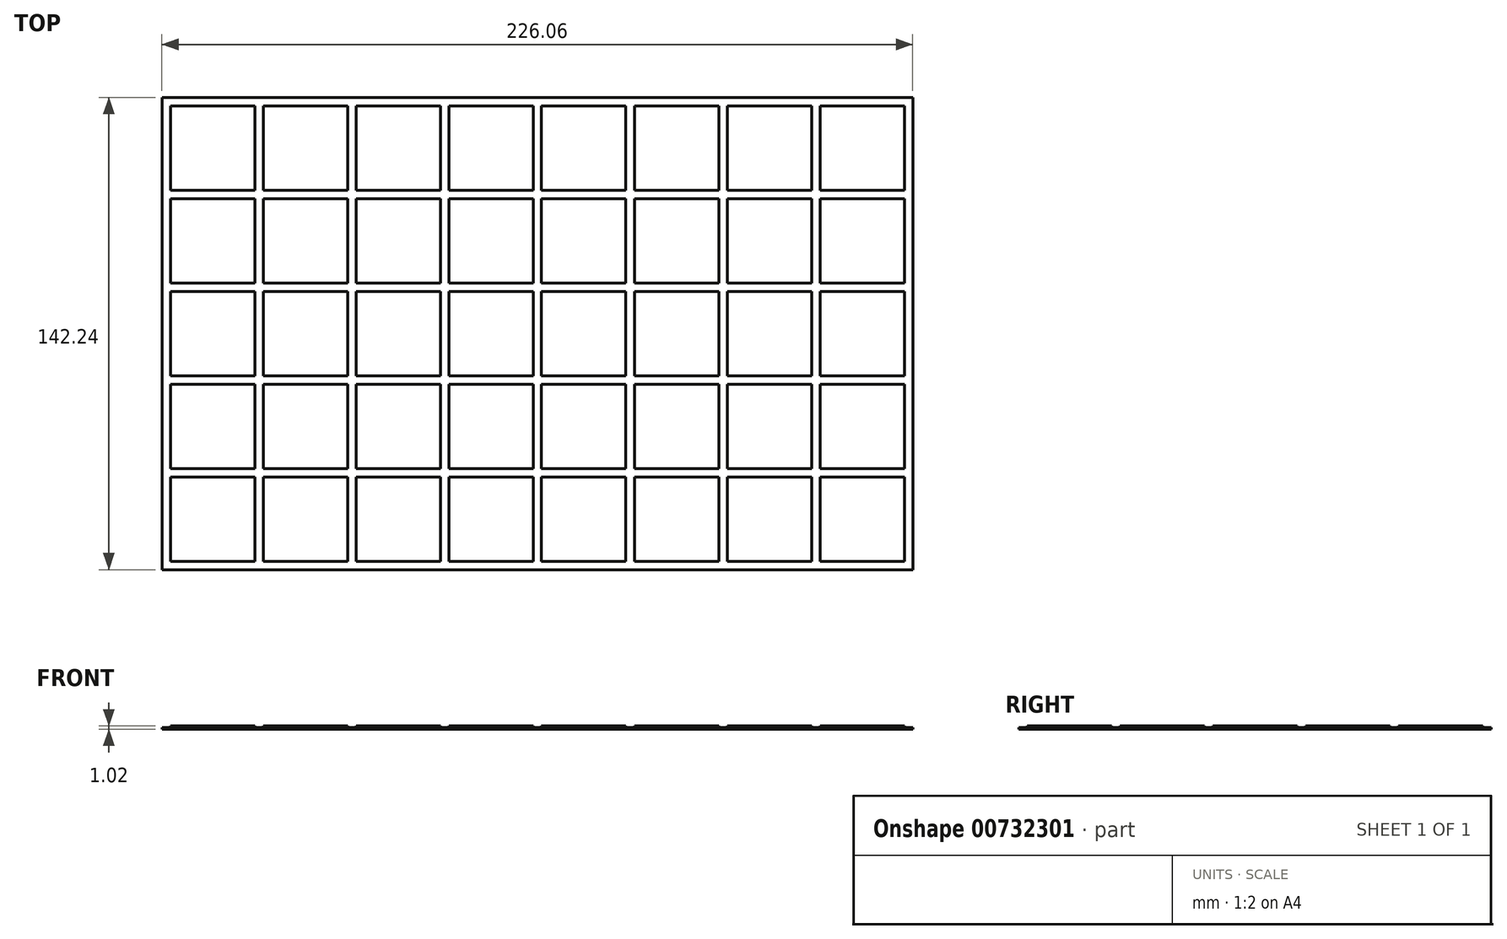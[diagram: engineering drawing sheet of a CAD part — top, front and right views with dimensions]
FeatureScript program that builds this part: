
annotation { "Feature Type Name" : "Feature", "Feature Type Description" : "" }
export const myFeature = defineFeature(function(context is Context, id is Id, definition is map)
    precondition{}
    {
        {
            var Q0;
            Q0=qCreatedBy(makeId("Top.planeOp"),FACE);
            var sketch = newSketch(context, id + "F0", { "sketchPlane" : qUnion([Q0])});
            skLineSegment(sketch, "E0.bottom", {"start": v(-100.86, 89.45) * mm, "end": v(125.2, 89.45) * mm});
            skLineSegment(sketch, "E0.top", {"start": v(-100.86, -52.79) * mm, "end": v(125.2, -52.79) * mm});
            skLineSegment(sketch, "E0.left", {"start": v(-100.86, 89.45) * mm, "end": v(-100.86, -52.79) * mm});
            skLineSegment(sketch, "E0.right", {"start": v(125.2, 89.45) * mm, "end": v(125.2, -52.79) * mm});
            skLineSegment(sketch, "E1.bottom", {"start": v(-98.32, -50.25) * mm, "end": v(-72.92, -50.25) * mm});
            skLineSegment(sketch, "E1.top", {"start": v(-98.32, -24.85) * mm, "end": v(-72.92, -24.85) * mm});
            skLineSegment(sketch, "E1.left", {"start": v(-98.32, -50.25) * mm, "end": v(-98.32, -24.85) * mm});
            skLineSegment(sketch, "E1.right", {"start": v(-72.92, -50.25) * mm, "end": v(-72.92, -24.85) * mm});
            skLineSegment(sketch, "E2.0.1.0", {"start": v(-72.92, -22.3) * mm, "end": v(-72.92, 3.1) * mm});
            skLineSegment(sketch, "E2.0.1.1", {"start": v(-98.32, 3.1) * mm, "end": v(-72.92, 3.1) * mm});
            skLineSegment(sketch, "E2.0.1.2", {"start": v(-98.32, -22.3) * mm, "end": v(-98.32, 3.1) * mm});
            skLineSegment(sketch, "E2.0.1.3", {"start": v(-98.32, -22.3) * mm, "end": v(-72.92, -22.3) * mm});
            skLineSegment(sketch, "E2.0.2.0", {"start": v(-72.92, 5.63) * mm, "end": v(-72.92, 31.03) * mm});
            skLineSegment(sketch, "E2.0.2.1", {"start": v(-98.32, 31.03) * mm, "end": v(-72.92, 31.03) * mm});
            skLineSegment(sketch, "E2.0.2.2", {"start": v(-98.32, 5.63) * mm, "end": v(-98.32, 31.03) * mm});
            skLineSegment(sketch, "E2.0.2.3", {"start": v(-98.32, 5.63) * mm, "end": v(-72.92, 5.63) * mm});
            skLineSegment(sketch, "E2.0.3.0", {"start": v(-72.92, 33.57) * mm, "end": v(-72.92, 58.97) * mm});
            skLineSegment(sketch, "E2.0.3.1", {"start": v(-98.32, 58.97) * mm, "end": v(-72.92, 58.97) * mm});
            skLineSegment(sketch, "E2.0.3.2", {"start": v(-98.32, 33.57) * mm, "end": v(-98.32, 58.97) * mm});
            skLineSegment(sketch, "E2.0.3.3", {"start": v(-98.32, 33.57) * mm, "end": v(-72.92, 33.57) * mm});
            skLineSegment(sketch, "E2.0.4.0", {"start": v(-72.92, 61.51) * mm, "end": v(-72.92, 86.91) * mm});
            skLineSegment(sketch, "E2.0.4.1", {"start": v(-98.32, 86.91) * mm, "end": v(-72.92, 86.91) * mm});
            skLineSegment(sketch, "E2.0.4.2", {"start": v(-98.32, 61.51) * mm, "end": v(-98.32, 86.91) * mm});
            skLineSegment(sketch, "E2.0.4.3", {"start": v(-98.32, 61.51) * mm, "end": v(-72.92, 61.51) * mm});
            skLineSegment(sketch, "E2.1.0.0", {"start": v(-44.98, -50.25) * mm, "end": v(-44.98, -24.85) * mm});
            skLineSegment(sketch, "E2.1.0.1", {"start": v(-70.38, -24.85) * mm, "end": v(-44.98, -24.85) * mm});
            skLineSegment(sketch, "E2.1.0.2", {"start": v(-70.38, -50.25) * mm, "end": v(-70.38, -24.85) * mm});
            skLineSegment(sketch, "E2.1.0.3", {"start": v(-70.38, -50.25) * mm, "end": v(-44.98, -50.25) * mm});
            skLineSegment(sketch, "E2.1.1.0", {"start": v(-44.98, -22.3) * mm, "end": v(-44.98, 3.1) * mm});
            skLineSegment(sketch, "E2.1.1.1", {"start": v(-70.38, 3.1) * mm, "end": v(-44.98, 3.1) * mm});
            skLineSegment(sketch, "E2.1.1.2", {"start": v(-70.38, -22.3) * mm, "end": v(-70.38, 3.1) * mm});
            skLineSegment(sketch, "E2.1.1.3", {"start": v(-70.38, -22.3) * mm, "end": v(-44.98, -22.3) * mm});
            skLineSegment(sketch, "E2.1.2.0", {"start": v(-44.98, 5.63) * mm, "end": v(-44.98, 31.03) * mm});
            skLineSegment(sketch, "E2.1.2.1", {"start": v(-70.38, 31.03) * mm, "end": v(-44.98, 31.03) * mm});
            skLineSegment(sketch, "E2.1.2.2", {"start": v(-70.38, 5.63) * mm, "end": v(-70.38, 31.03) * mm});
            skLineSegment(sketch, "E2.1.2.3", {"start": v(-70.38, 5.63) * mm, "end": v(-44.98, 5.63) * mm});
            skLineSegment(sketch, "E2.1.3.0", {"start": v(-44.98, 33.57) * mm, "end": v(-44.98, 58.97) * mm});
            skLineSegment(sketch, "E2.1.3.1", {"start": v(-70.38, 58.97) * mm, "end": v(-44.98, 58.97) * mm});
            skLineSegment(sketch, "E2.1.3.2", {"start": v(-70.38, 33.57) * mm, "end": v(-70.38, 58.97) * mm});
            skLineSegment(sketch, "E2.1.3.3", {"start": v(-70.38, 33.57) * mm, "end": v(-44.98, 33.57) * mm});
            skLineSegment(sketch, "E2.1.4.0", {"start": v(-44.98, 61.51) * mm, "end": v(-44.98, 86.91) * mm});
            skLineSegment(sketch, "E2.1.4.1", {"start": v(-70.38, 86.91) * mm, "end": v(-44.98, 86.91) * mm});
            skLineSegment(sketch, "E2.1.4.2", {"start": v(-70.38, 61.51) * mm, "end": v(-70.38, 86.91) * mm});
            skLineSegment(sketch, "E2.1.4.3", {"start": v(-70.38, 61.51) * mm, "end": v(-44.98, 61.51) * mm});
            skLineSegment(sketch, "E2.2.0.0", {"start": v(-17.04, -50.25) * mm, "end": v(-17.04, -24.85) * mm});
            skLineSegment(sketch, "E2.2.0.1", {"start": v(-42.44, -24.85) * mm, "end": v(-17.04, -24.85) * mm});
            skLineSegment(sketch, "E2.2.0.2", {"start": v(-42.44, -50.25) * mm, "end": v(-42.44, -24.85) * mm});
            skLineSegment(sketch, "E2.2.0.3", {"start": v(-42.44, -50.25) * mm, "end": v(-17.04, -50.25) * mm});
            skLineSegment(sketch, "E2.2.1.0", {"start": v(-17.04, -22.3) * mm, "end": v(-17.04, 3.1) * mm});
            skLineSegment(sketch, "E2.2.1.1", {"start": v(-42.44, 3.1) * mm, "end": v(-17.04, 3.1) * mm});
            skLineSegment(sketch, "E2.2.1.2", {"start": v(-42.44, -22.3) * mm, "end": v(-42.44, 3.1) * mm});
            skLineSegment(sketch, "E2.2.1.3", {"start": v(-42.44, -22.3) * mm, "end": v(-17.04, -22.3) * mm});
            skLineSegment(sketch, "E2.2.2.0", {"start": v(-17.04, 5.63) * mm, "end": v(-17.04, 31.03) * mm});
            skLineSegment(sketch, "E2.2.2.1", {"start": v(-42.44, 31.03) * mm, "end": v(-17.04, 31.03) * mm});
            skLineSegment(sketch, "E2.2.2.2", {"start": v(-42.44, 5.63) * mm, "end": v(-42.44, 31.03) * mm});
            skLineSegment(sketch, "E2.2.2.3", {"start": v(-42.44, 5.63) * mm, "end": v(-17.04, 5.63) * mm});
            skLineSegment(sketch, "E2.2.3.0", {"start": v(-17.04, 33.57) * mm, "end": v(-17.04, 58.97) * mm});
            skLineSegment(sketch, "E2.2.3.1", {"start": v(-42.44, 58.97) * mm, "end": v(-17.04, 58.97) * mm});
            skLineSegment(sketch, "E2.2.3.2", {"start": v(-42.44, 33.57) * mm, "end": v(-42.44, 58.97) * mm});
            skLineSegment(sketch, "E2.2.3.3", {"start": v(-42.44, 33.57) * mm, "end": v(-17.04, 33.57) * mm});
            skLineSegment(sketch, "E2.2.4.0", {"start": v(-17.04, 61.51) * mm, "end": v(-17.04, 86.91) * mm});
            skLineSegment(sketch, "E2.2.4.1", {"start": v(-42.44, 86.91) * mm, "end": v(-17.04, 86.91) * mm});
            skLineSegment(sketch, "E2.2.4.2", {"start": v(-42.44, 61.51) * mm, "end": v(-42.44, 86.91) * mm});
            skLineSegment(sketch, "E2.2.4.3", {"start": v(-42.44, 61.51) * mm, "end": v(-17.04, 61.51) * mm});
            skLineSegment(sketch, "E2.3.0.0", {"start": v(10.9, -50.25) * mm, "end": v(10.9, -24.85) * mm});
            skLineSegment(sketch, "E2.3.0.1", {"start": v(-14.5, -24.85) * mm, "end": v(10.9, -24.85) * mm});
            skLineSegment(sketch, "E2.3.0.2", {"start": v(-14.5, -50.25) * mm, "end": v(-14.5, -24.85) * mm});
            skLineSegment(sketch, "E2.3.0.3", {"start": v(-14.5, -50.25) * mm, "end": v(10.9, -50.25) * mm});
            skLineSegment(sketch, "E2.3.1.0", {"start": v(10.9, -22.3) * mm, "end": v(10.9, 3.1) * mm});
            skLineSegment(sketch, "E2.3.1.1", {"start": v(-14.5, 3.1) * mm, "end": v(10.9, 3.1) * mm});
            skLineSegment(sketch, "E2.3.1.2", {"start": v(-14.5, -22.3) * mm, "end": v(-14.5, 3.1) * mm});
            skLineSegment(sketch, "E2.3.1.3", {"start": v(-14.5, -22.3) * mm, "end": v(10.9, -22.3) * mm});
            skLineSegment(sketch, "E2.3.2.0", {"start": v(10.9, 5.63) * mm, "end": v(10.9, 31.03) * mm});
            skLineSegment(sketch, "E2.3.2.1", {"start": v(-14.5, 31.03) * mm, "end": v(10.9, 31.03) * mm});
            skLineSegment(sketch, "E2.3.2.2", {"start": v(-14.5, 5.63) * mm, "end": v(-14.5, 31.03) * mm});
            skLineSegment(sketch, "E2.3.2.3", {"start": v(-14.5, 5.63) * mm, "end": v(10.9, 5.63) * mm});
            skLineSegment(sketch, "E2.3.3.0", {"start": v(10.9, 33.57) * mm, "end": v(10.9, 58.97) * mm});
            skLineSegment(sketch, "E2.3.3.1", {"start": v(-14.5, 58.97) * mm, "end": v(10.9, 58.97) * mm});
            skLineSegment(sketch, "E2.3.3.2", {"start": v(-14.5, 33.57) * mm, "end": v(-14.5, 58.97) * mm});
            skLineSegment(sketch, "E2.3.3.3", {"start": v(-14.5, 33.57) * mm, "end": v(10.9, 33.57) * mm});
            skLineSegment(sketch, "E2.3.4.0", {"start": v(10.9, 61.51) * mm, "end": v(10.9, 86.91) * mm});
            skLineSegment(sketch, "E2.3.4.1", {"start": v(-14.5, 86.91) * mm, "end": v(10.9, 86.91) * mm});
            skLineSegment(sketch, "E2.3.4.2", {"start": v(-14.5, 61.51) * mm, "end": v(-14.5, 86.91) * mm});
            skLineSegment(sketch, "E2.3.4.3", {"start": v(-14.5, 61.51) * mm, "end": v(10.9, 61.51) * mm});
            skLineSegment(sketch, "E2.4.0.0", {"start": v(38.84, -50.25) * mm, "end": v(38.84, -24.85) * mm});
            skLineSegment(sketch, "E2.4.0.1", {"start": v(13.44, -24.85) * mm, "end": v(38.84, -24.85) * mm});
            skLineSegment(sketch, "E2.4.0.2", {"start": v(13.44, -50.25) * mm, "end": v(13.44, -24.85) * mm});
            skLineSegment(sketch, "E2.4.0.3", {"start": v(13.44, -50.25) * mm, "end": v(38.84, -50.25) * mm});
            skLineSegment(sketch, "E2.4.1.0", {"start": v(38.84, -22.3) * mm, "end": v(38.84, 3.1) * mm});
            skLineSegment(sketch, "E2.4.1.1", {"start": v(13.44, 3.1) * mm, "end": v(38.84, 3.1) * mm});
            skLineSegment(sketch, "E2.4.1.2", {"start": v(13.44, -22.3) * mm, "end": v(13.44, 3.1) * mm});
            skLineSegment(sketch, "E2.4.1.3", {"start": v(13.44, -22.3) * mm, "end": v(38.84, -22.3) * mm});
            skLineSegment(sketch, "E2.4.2.0", {"start": v(38.84, 5.63) * mm, "end": v(38.84, 31.03) * mm});
            skLineSegment(sketch, "E2.4.2.1", {"start": v(13.44, 31.03) * mm, "end": v(38.84, 31.03) * mm});
            skLineSegment(sketch, "E2.4.2.2", {"start": v(13.44, 5.63) * mm, "end": v(13.44, 31.03) * mm});
            skLineSegment(sketch, "E2.4.2.3", {"start": v(13.44, 5.63) * mm, "end": v(38.84, 5.63) * mm});
            skLineSegment(sketch, "E2.4.3.0", {"start": v(38.84, 33.57) * mm, "end": v(38.84, 58.97) * mm});
            skLineSegment(sketch, "E2.4.3.1", {"start": v(13.44, 58.97) * mm, "end": v(38.84, 58.97) * mm});
            skLineSegment(sketch, "E2.4.3.2", {"start": v(13.44, 33.57) * mm, "end": v(13.44, 58.97) * mm});
            skLineSegment(sketch, "E2.4.3.3", {"start": v(13.44, 33.57) * mm, "end": v(38.84, 33.57) * mm});
            skLineSegment(sketch, "E2.4.4.0", {"start": v(38.84, 61.51) * mm, "end": v(38.84, 86.91) * mm});
            skLineSegment(sketch, "E2.4.4.1", {"start": v(13.44, 86.91) * mm, "end": v(38.84, 86.91) * mm});
            skLineSegment(sketch, "E2.4.4.2", {"start": v(13.44, 61.51) * mm, "end": v(13.44, 86.91) * mm});
            skLineSegment(sketch, "E2.4.4.3", {"start": v(13.44, 61.51) * mm, "end": v(38.84, 61.51) * mm});
            skLineSegment(sketch, "E2.5.0.0", {"start": v(66.78, -50.25) * mm, "end": v(66.78, -24.85) * mm});
            skLineSegment(sketch, "E2.5.0.1", {"start": v(41.38, -24.85) * mm, "end": v(66.78, -24.85) * mm});
            skLineSegment(sketch, "E2.5.0.2", {"start": v(41.38, -50.25) * mm, "end": v(41.38, -24.85) * mm});
            skLineSegment(sketch, "E2.5.0.3", {"start": v(41.38, -50.25) * mm, "end": v(66.78, -50.25) * mm});
            skLineSegment(sketch, "E2.5.1.0", {"start": v(66.78, -22.3) * mm, "end": v(66.78, 3.1) * mm});
            skLineSegment(sketch, "E2.5.1.1", {"start": v(41.38, 3.1) * mm, "end": v(66.78, 3.1) * mm});
            skLineSegment(sketch, "E2.5.1.2", {"start": v(41.38, -22.3) * mm, "end": v(41.38, 3.1) * mm});
            skLineSegment(sketch, "E2.5.1.3", {"start": v(41.38, -22.3) * mm, "end": v(66.78, -22.3) * mm});
            skLineSegment(sketch, "E2.5.2.0", {"start": v(66.78, 5.63) * mm, "end": v(66.78, 31.03) * mm});
            skLineSegment(sketch, "E2.5.2.1", {"start": v(41.38, 31.03) * mm, "end": v(66.78, 31.03) * mm});
            skLineSegment(sketch, "E2.5.2.2", {"start": v(41.38, 5.63) * mm, "end": v(41.38, 31.03) * mm});
            skLineSegment(sketch, "E2.5.2.3", {"start": v(41.38, 5.63) * mm, "end": v(66.78, 5.63) * mm});
            skLineSegment(sketch, "E2.5.3.0", {"start": v(66.78, 33.57) * mm, "end": v(66.78, 58.97) * mm});
            skLineSegment(sketch, "E2.5.3.1", {"start": v(41.38, 58.97) * mm, "end": v(66.78, 58.97) * mm});
            skLineSegment(sketch, "E2.5.3.2", {"start": v(41.38, 33.57) * mm, "end": v(41.38, 58.97) * mm});
            skLineSegment(sketch, "E2.5.3.3", {"start": v(41.38, 33.57) * mm, "end": v(66.78, 33.57) * mm});
            skLineSegment(sketch, "E2.5.4.0", {"start": v(66.78, 61.51) * mm, "end": v(66.78, 86.91) * mm});
            skLineSegment(sketch, "E2.5.4.1", {"start": v(41.38, 86.91) * mm, "end": v(66.78, 86.91) * mm});
            skLineSegment(sketch, "E2.5.4.2", {"start": v(41.38, 61.51) * mm, "end": v(41.38, 86.91) * mm});
            skLineSegment(sketch, "E2.5.4.3", {"start": v(41.38, 61.51) * mm, "end": v(66.78, 61.51) * mm});
            skLineSegment(sketch, "E2.6.0.0", {"start": v(94.72, -50.25) * mm, "end": v(94.72, -24.85) * mm});
            skLineSegment(sketch, "E2.6.0.1", {"start": v(69.32, -24.85) * mm, "end": v(94.72, -24.85) * mm});
            skLineSegment(sketch, "E2.6.0.2", {"start": v(69.32, -50.25) * mm, "end": v(69.32, -24.85) * mm});
            skLineSegment(sketch, "E2.6.0.3", {"start": v(69.32, -50.25) * mm, "end": v(94.72, -50.25) * mm});
            skLineSegment(sketch, "E2.6.1.0", {"start": v(94.72, -22.3) * mm, "end": v(94.72, 3.1) * mm});
            skLineSegment(sketch, "E2.6.1.1", {"start": v(69.32, 3.1) * mm, "end": v(94.72, 3.1) * mm});
            skLineSegment(sketch, "E2.6.1.2", {"start": v(69.32, -22.3) * mm, "end": v(69.32, 3.1) * mm});
            skLineSegment(sketch, "E2.6.1.3", {"start": v(69.32, -22.3) * mm, "end": v(94.72, -22.3) * mm});
            skLineSegment(sketch, "E2.6.2.0", {"start": v(94.72, 5.63) * mm, "end": v(94.72, 31.03) * mm});
            skLineSegment(sketch, "E2.6.2.1", {"start": v(69.32, 31.03) * mm, "end": v(94.72, 31.03) * mm});
            skLineSegment(sketch, "E2.6.2.2", {"start": v(69.32, 5.63) * mm, "end": v(69.32, 31.03) * mm});
            skLineSegment(sketch, "E2.6.2.3", {"start": v(69.32, 5.63) * mm, "end": v(94.72, 5.63) * mm});
            skLineSegment(sketch, "E2.6.3.0", {"start": v(94.72, 33.57) * mm, "end": v(94.72, 58.97) * mm});
            skLineSegment(sketch, "E2.6.3.1", {"start": v(69.32, 58.97) * mm, "end": v(94.72, 58.97) * mm});
            skLineSegment(sketch, "E2.6.3.2", {"start": v(69.32, 33.57) * mm, "end": v(69.32, 58.97) * mm});
            skLineSegment(sketch, "E2.6.3.3", {"start": v(69.32, 33.57) * mm, "end": v(94.72, 33.57) * mm});
            skLineSegment(sketch, "E2.6.4.0", {"start": v(94.72, 61.51) * mm, "end": v(94.72, 86.91) * mm});
            skLineSegment(sketch, "E2.6.4.1", {"start": v(69.32, 86.91) * mm, "end": v(94.72, 86.91) * mm});
            skLineSegment(sketch, "E2.6.4.2", {"start": v(69.32, 61.51) * mm, "end": v(69.32, 86.91) * mm});
            skLineSegment(sketch, "E2.6.4.3", {"start": v(69.32, 61.51) * mm, "end": v(94.72, 61.51) * mm});
            skLineSegment(sketch, "E2.7.0.0", {"start": v(122.66, -50.25) * mm, "end": v(122.66, -24.85) * mm});
            skLineSegment(sketch, "E2.7.0.1", {"start": v(97.26, -24.85) * mm, "end": v(122.66, -24.85) * mm});
            skLineSegment(sketch, "E2.7.0.2", {"start": v(97.26, -50.25) * mm, "end": v(97.26, -24.85) * mm});
            skLineSegment(sketch, "E2.7.0.3", {"start": v(97.26, -50.25) * mm, "end": v(122.66, -50.25) * mm});
            skLineSegment(sketch, "E2.7.1.0", {"start": v(122.66, -22.3) * mm, "end": v(122.66, 3.1) * mm});
            skLineSegment(sketch, "E2.7.1.1", {"start": v(97.26, 3.1) * mm, "end": v(122.66, 3.1) * mm});
            skLineSegment(sketch, "E2.7.1.2", {"start": v(97.26, -22.3) * mm, "end": v(97.26, 3.1) * mm});
            skLineSegment(sketch, "E2.7.1.3", {"start": v(97.26, -22.3) * mm, "end": v(122.66, -22.3) * mm});
            skLineSegment(sketch, "E2.7.2.0", {"start": v(122.66, 5.63) * mm, "end": v(122.66, 31.03) * mm});
            skLineSegment(sketch, "E2.7.2.1", {"start": v(97.26, 31.03) * mm, "end": v(122.66, 31.03) * mm});
            skLineSegment(sketch, "E2.7.2.2", {"start": v(97.26, 5.63) * mm, "end": v(97.26, 31.03) * mm});
            skLineSegment(sketch, "E2.7.2.3", {"start": v(97.26, 5.63) * mm, "end": v(122.66, 5.63) * mm});
            skLineSegment(sketch, "E2.7.3.0", {"start": v(122.66, 33.57) * mm, "end": v(122.66, 58.97) * mm});
            skLineSegment(sketch, "E2.7.3.1", {"start": v(97.26, 58.97) * mm, "end": v(122.66, 58.97) * mm});
            skLineSegment(sketch, "E2.7.3.2", {"start": v(97.26, 33.57) * mm, "end": v(97.26, 58.97) * mm});
            skLineSegment(sketch, "E2.7.3.3", {"start": v(97.26, 33.57) * mm, "end": v(122.66, 33.57) * mm});
            skLineSegment(sketch, "E2.7.4.0", {"start": v(122.66, 61.51) * mm, "end": v(122.66, 86.91) * mm});
            skLineSegment(sketch, "E2.7.4.1", {"start": v(97.26, 86.91) * mm, "end": v(122.66, 86.91) * mm});
            skLineSegment(sketch, "E2.7.4.2", {"start": v(97.26, 61.51) * mm, "end": v(97.26, 86.91) * mm});
            skLineSegment(sketch, "E2.7.4.3", {"start": v(97.26, 61.51) * mm, "end": v(122.66, 61.51) * mm});
            skLineSegment(sketch, "E2.direction1", {"start": v(-72.92, -50.25) * mm, "end": v(-44.98, -50.25) * mm, "construction": true});
            skLineSegment(sketch, "E2.direction2", {"start": v(-72.92, -50.25) * mm, "end": v(-72.92, -22.3) * mm, "construction": true});
            skSolve(sketch);
        }
        {
            var Q0;
            Q0=makeQuery(id+"F0.imprint","IMPRINT",FACE,{"disambiguationData":[TD([[makeQuery(id+"F0.imprint","IMPRINT",EDGE,{"derivedFrom":sQuery(id+"F0.wireOp",EDGE,"E0.bottom")}),-1.0]])]});
            extrude(context, id + "F1", {"entities" : qUnion([Q0]), "depth" : 0.5 * mm, "offsetDistance" : 25.4 * mm});
        }
        {
            var Q0;
            Q0=makeQuery(id+"F0.imprint","IMPRINT",FACE,{"disambiguationData":[TD([[makeQuery(id+"F0.imprint","IMPRINT",EDGE,{"derivedFrom":sQuery(id+"F0.wireOp",EDGE,"E2.0.2.0")}),1.0]])]});
            var Q1;
            Q1=makeQuery(id+"F0.imprint","IMPRINT",FACE,{"disambiguationData":[TD([[makeQuery(id+"F0.imprint","IMPRINT",EDGE,{"derivedFrom":sQuery(id+"F0.wireOp",EDGE,"E2.1.2.0")}),1.0]])]});
            var Q2;
            Q2=makeQuery(id+"F0.imprint","IMPRINT",FACE,{"disambiguationData":[TD([[makeQuery(id+"F0.imprint","IMPRINT",EDGE,{"derivedFrom":sQuery(id+"F0.wireOp",EDGE,"E2.1.3.0")}),1.0]])]});
            var Q3;
            Q3=makeQuery(id+"F0.imprint","IMPRINT",FACE,{"disambiguationData":[TD([[makeQuery(id+"F0.imprint","IMPRINT",EDGE,{"derivedFrom":sQuery(id+"F0.wireOp",EDGE,"E2.0.3.0")}),1.0]])]});
            var Q4;
            Q4=makeQuery(id+"F0.imprint","IMPRINT",FACE,{"disambiguationData":[TD([[makeQuery(id+"F0.imprint","IMPRINT",EDGE,{"derivedFrom":sQuery(id+"F0.wireOp",EDGE,"E2.0.4.0")}),1.0]])]});
            var Q5;
            Q5=makeQuery(id+"F0.imprint","IMPRINT",FACE,{"disambiguationData":[TD([[makeQuery(id+"F0.imprint","IMPRINT",EDGE,{"derivedFrom":sQuery(id+"F0.wireOp",EDGE,"E2.1.4.0")}),1.0]])]});
            var Q6;
            Q6=makeQuery(id+"F0.imprint","IMPRINT",FACE,{"disambiguationData":[TD([[makeQuery(id+"F0.imprint","IMPRINT",EDGE,{"derivedFrom":sQuery(id+"F0.wireOp",EDGE,"E2.0.1.0")}),1.0]])]});
            var Q7;
            Q7=makeQuery(id+"F0.imprint","IMPRINT",FACE,{"disambiguationData":[TD([[makeQuery(id+"F0.imprint","IMPRINT",EDGE,{"derivedFrom":sQuery(id+"F0.wireOp",EDGE,"E2.1.1.0")}),1.0]])]});
            var Q8;
            Q8=makeQuery(id+"F0.imprint","IMPRINT",FACE,{"disambiguationData":[TD([[makeQuery(id+"F0.imprint","IMPRINT",EDGE,{"derivedFrom":sQuery(id+"F0.wireOp",EDGE,"E2.1.0.0")}),1.0]])]});
            var Q9;
            Q9=makeQuery(id+"F0.imprint","IMPRINT",FACE,{"disambiguationData":[TD([[makeQuery(id+"F0.imprint","IMPRINT",EDGE,{"derivedFrom":sQuery(id+"F0.wireOp",EDGE,"E1.bottom")}),1.0]])]});
            var Q10;
            Q10=makeQuery(id+"F0.imprint","IMPRINT",FACE,{"disambiguationData":[TD([[makeQuery(id+"F0.imprint","IMPRINT",EDGE,{"derivedFrom":sQuery(id+"F0.wireOp",EDGE,"E2.2.0.0")}),1.0]])]});
            var Q11;
            Q11=makeQuery(id+"F0.imprint","IMPRINT",FACE,{"disambiguationData":[TD([[makeQuery(id+"F0.imprint","IMPRINT",EDGE,{"derivedFrom":sQuery(id+"F0.wireOp",EDGE,"E2.2.1.0")}),1.0]])]});
            var Q12;
            Q12=makeQuery(id+"F0.imprint","IMPRINT",FACE,{"disambiguationData":[TD([[makeQuery(id+"F0.imprint","IMPRINT",EDGE,{"derivedFrom":sQuery(id+"F0.wireOp",EDGE,"E2.2.2.0")}),1.0]])]});
            var Q13;
            Q13=makeQuery(id+"F0.imprint","IMPRINT",FACE,{"disambiguationData":[TD([[makeQuery(id+"F0.imprint","IMPRINT",EDGE,{"derivedFrom":sQuery(id+"F0.wireOp",EDGE,"E2.2.3.0")}),1.0]])]});
            var Q14;
            Q14=makeQuery(id+"F0.imprint","IMPRINT",FACE,{"disambiguationData":[TD([[makeQuery(id+"F0.imprint","IMPRINT",EDGE,{"derivedFrom":sQuery(id+"F0.wireOp",EDGE,"E2.2.4.0")}),1.0]])]});
            var Q15;
            Q15=makeQuery(id+"F0.imprint","IMPRINT",FACE,{"disambiguationData":[TD([[makeQuery(id+"F0.imprint","IMPRINT",EDGE,{"derivedFrom":sQuery(id+"F0.wireOp",EDGE,"E2.3.4.0")}),1.0]])]});
            var Q16;
            Q16=makeQuery(id+"F0.imprint","IMPRINT",FACE,{"disambiguationData":[TD([[makeQuery(id+"F0.imprint","IMPRINT",EDGE,{"derivedFrom":sQuery(id+"F0.wireOp",EDGE,"E2.3.3.0")}),1.0]])]});
            var Q17;
            Q17=makeQuery(id+"F0.imprint","IMPRINT",FACE,{"disambiguationData":[TD([[makeQuery(id+"F0.imprint","IMPRINT",EDGE,{"derivedFrom":sQuery(id+"F0.wireOp",EDGE,"E2.3.2.0")}),1.0]])]});
            var Q18;
            Q18=makeQuery(id+"F0.imprint","IMPRINT",FACE,{"disambiguationData":[TD([[makeQuery(id+"F0.imprint","IMPRINT",EDGE,{"derivedFrom":sQuery(id+"F0.wireOp",EDGE,"E2.3.1.0")}),1.0]])]});
            var Q19;
            Q19=makeQuery(id+"F0.imprint","IMPRINT",FACE,{"disambiguationData":[TD([[makeQuery(id+"F0.imprint","IMPRINT",EDGE,{"derivedFrom":sQuery(id+"F0.wireOp",EDGE,"E2.3.0.0")}),1.0]])]});
            var Q20;
            Q20=makeQuery(id+"F0.imprint","IMPRINT",FACE,{"disambiguationData":[TD([[makeQuery(id+"F0.imprint","IMPRINT",EDGE,{"derivedFrom":sQuery(id+"F0.wireOp",EDGE,"E2.4.0.0")}),1.0]])]});
            var Q21;
            Q21=makeQuery(id+"F0.imprint","IMPRINT",FACE,{"disambiguationData":[TD([[makeQuery(id+"F0.imprint","IMPRINT",EDGE,{"derivedFrom":sQuery(id+"F0.wireOp",EDGE,"E2.4.1.0")}),1.0]])]});
            var Q22;
            Q22=makeQuery(id+"F0.imprint","IMPRINT",FACE,{"disambiguationData":[TD([[makeQuery(id+"F0.imprint","IMPRINT",EDGE,{"derivedFrom":sQuery(id+"F0.wireOp",EDGE,"E2.4.2.0")}),1.0]])]});
            var Q23;
            Q23=makeQuery(id+"F0.imprint","IMPRINT",FACE,{"disambiguationData":[TD([[makeQuery(id+"F0.imprint","IMPRINT",EDGE,{"derivedFrom":sQuery(id+"F0.wireOp",EDGE,"E2.4.3.0")}),1.0]])]});
            var Q24;
            Q24=makeQuery(id+"F0.imprint","IMPRINT",FACE,{"disambiguationData":[TD([[makeQuery(id+"F0.imprint","IMPRINT",EDGE,{"derivedFrom":sQuery(id+"F0.wireOp",EDGE,"E2.4.4.0")}),1.0]])]});
            var Q25;
            Q25=makeQuery(id+"F0.imprint","IMPRINT",FACE,{"disambiguationData":[TD([[makeQuery(id+"F0.imprint","IMPRINT",EDGE,{"derivedFrom":sQuery(id+"F0.wireOp",EDGE,"E2.5.4.0")}),1.0]])]});
            var Q26;
            Q26=makeQuery(id+"F0.imprint","IMPRINT",FACE,{"disambiguationData":[TD([[makeQuery(id+"F0.imprint","IMPRINT",EDGE,{"derivedFrom":sQuery(id+"F0.wireOp",EDGE,"E2.5.3.0")}),1.0]])]});
            var Q27;
            Q27=makeQuery(id+"F0.imprint","IMPRINT",FACE,{"disambiguationData":[TD([[makeQuery(id+"F0.imprint","IMPRINT",EDGE,{"derivedFrom":sQuery(id+"F0.wireOp",EDGE,"E2.5.2.0")}),1.0]])]});
            var Q28;
            Q28=makeQuery(id+"F0.imprint","IMPRINT",FACE,{"disambiguationData":[TD([[makeQuery(id+"F0.imprint","IMPRINT",EDGE,{"derivedFrom":sQuery(id+"F0.wireOp",EDGE,"E2.5.1.0")}),1.0]])]});
            var Q29;
            Q29=makeQuery(id+"F0.imprint","IMPRINT",FACE,{"disambiguationData":[TD([[makeQuery(id+"F0.imprint","IMPRINT",EDGE,{"derivedFrom":sQuery(id+"F0.wireOp",EDGE,"E2.5.0.0")}),1.0]])]});
            var Q30;
            Q30=makeQuery(id+"F0.imprint","IMPRINT",FACE,{"disambiguationData":[TD([[makeQuery(id+"F0.imprint","IMPRINT",EDGE,{"derivedFrom":sQuery(id+"F0.wireOp",EDGE,"E2.6.0.0")}),1.0]])]});
            var Q31;
            Q31=makeQuery(id+"F0.imprint","IMPRINT",FACE,{"disambiguationData":[TD([[makeQuery(id+"F0.imprint","IMPRINT",EDGE,{"derivedFrom":sQuery(id+"F0.wireOp",EDGE,"E2.6.1.0")}),1.0]])]});
            var Q32;
            Q32=makeQuery(id+"F0.imprint","IMPRINT",FACE,{"disambiguationData":[TD([[makeQuery(id+"F0.imprint","IMPRINT",EDGE,{"derivedFrom":sQuery(id+"F0.wireOp",EDGE,"E2.6.2.0")}),1.0]])]});
            var Q33;
            Q33=makeQuery(id+"F0.imprint","IMPRINT",FACE,{"disambiguationData":[TD([[makeQuery(id+"F0.imprint","IMPRINT",EDGE,{"derivedFrom":sQuery(id+"F0.wireOp",EDGE,"E2.6.3.0")}),1.0]])]});
            var Q34;
            Q34=makeQuery(id+"F0.imprint","IMPRINT",FACE,{"disambiguationData":[TD([[makeQuery(id+"F0.imprint","IMPRINT",EDGE,{"derivedFrom":sQuery(id+"F0.wireOp",EDGE,"E2.6.4.0")}),1.0]])]});
            var Q35;
            Q35=makeQuery(id+"F0.imprint","IMPRINT",FACE,{"disambiguationData":[TD([[makeQuery(id+"F0.imprint","IMPRINT",EDGE,{"derivedFrom":sQuery(id+"F0.wireOp",EDGE,"E2.7.4.0")}),1.0]])]});
            var Q36;
            Q36=makeQuery(id+"F0.imprint","IMPRINT",FACE,{"disambiguationData":[TD([[makeQuery(id+"F0.imprint","IMPRINT",EDGE,{"derivedFrom":sQuery(id+"F0.wireOp",EDGE,"E2.7.3.0")}),1.0]])]});
            var Q37;
            Q37=makeQuery(id+"F0.imprint","IMPRINT",FACE,{"disambiguationData":[TD([[makeQuery(id+"F0.imprint","IMPRINT",EDGE,{"derivedFrom":sQuery(id+"F0.wireOp",EDGE,"E2.7.2.0")}),1.0]])]});
            var Q38;
            Q38=makeQuery(id+"F0.imprint","IMPRINT",FACE,{"disambiguationData":[TD([[makeQuery(id+"F0.imprint","IMPRINT",EDGE,{"derivedFrom":sQuery(id+"F0.wireOp",EDGE,"E2.7.1.0")}),1.0]])]});
            var Q39;
            Q39=makeQuery(id+"F0.imprint","IMPRINT",FACE,{"disambiguationData":[TD([[makeQuery(id+"F0.imprint","IMPRINT",EDGE,{"derivedFrom":sQuery(id+"F0.wireOp",EDGE,"E2.7.0.0")}),1.0]])]});
            extrude(context, id + "F2", {"entities" : qUnion([Q0, Q1, Q2, Q3, Q4, Q5, Q6, Q7, Q8, Q9, Q10, Q11, Q12, Q13, Q14, Q15, Q16, Q17, Q18, Q19, Q20, Q21, Q22, Q23, Q24, Q25, Q26, Q27, Q28, Q29, Q30, Q31, Q32, Q33, Q34, Q35, Q36, Q37, Q38, Q39]), "operationType" : NewBodyOperationType.ADD, "depth" : 1.02 * mm, "offsetDistance" : 25.4 * mm});
        }
    });
